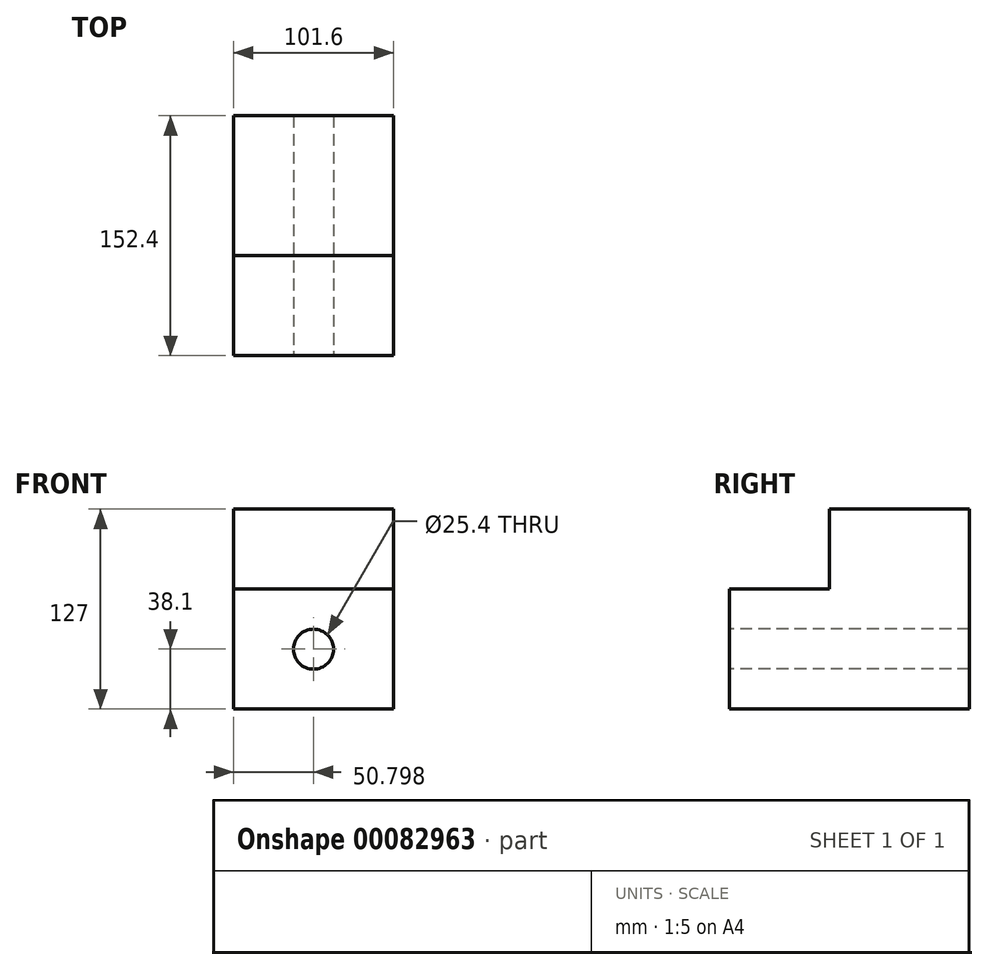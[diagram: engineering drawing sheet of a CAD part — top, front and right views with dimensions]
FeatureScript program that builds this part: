
annotation { "Feature Type Name" : "Feature", "Feature Type Description" : "" }
export const myFeature = defineFeature(function(context is Context, id is Id, definition is map)
    precondition{}
    {
        {
            var Q0;
            Q0=qCreatedBy(makeId("Top.planeOp"),FACE);
            var sketch = newSketch(context, id + "F0", { "sketchPlane" : qUnion([Q0])});
            skLineSegment(sketch, "E0.bottom", {"start": v(-16.71, 112.96) * mm, "end": v(84.89, 112.96) * mm});
            skLineSegment(sketch, "E0.top", {"start": v(-16.71, -39.44) * mm, "end": v(84.89, -39.44) * mm});
            skLineSegment(sketch, "E0.left", {"start": v(-16.71, 112.96) * mm, "end": v(-16.71, -39.44) * mm});
            skLineSegment(sketch, "E0.right", {"start": v(84.89, 112.96) * mm, "end": v(84.89, -39.44) * mm});
            skSolve(sketch);
        }
        {
            var Q0;
            Q0 = qSketchRegion(id + "F0", true);
            extrude(context, id + "F1", {"entities" : qUnion([Q0]), "depth" : 127 * mm});
        }
        {
            var Q0;
            Q0=makeQuery(id+"F1.opExtrude","SWEPT_FACE",FACE,{"disambiguationData":[OSD([sQuery(id+"F0.wireOp",EDGE,"E0.left")])]});
            var sketch = newSketch(context, id + "F2", { "sketchPlane" : qUnion([Q0])});
            skLineSegment(sketch, "E1.bottom", {"start": v(39.44, 127) * mm, "end": v(-24.06, 127) * mm});
            skLineSegment(sketch, "E1.top", {"start": v(39.44, 76.2) * mm, "end": v(-24.06, 76.2) * mm});
            skLineSegment(sketch, "E1.left", {"start": v(39.44, 127) * mm, "end": v(39.44, 76.2) * mm});
            skLineSegment(sketch, "E1.right", {"start": v(-24.06, 127) * mm, "end": v(-24.06, 76.2) * mm});
            skSolve(sketch);
        }
        {
            var Q0;
            Q0 = qSketchRegion(id + "F2", true);
            extrude(context, id + "F3", {"entities" : qUnion([Q0]), "operationType" : NewBodyOperationType.REMOVE, "oppositeDirection" : true, "depth" : 101.6 * mm});
        }
        {
            var Q0;
            Q0=makeQuery(id+"F1.opExtrude","SWEPT_FACE",FACE,{"disambiguationData":[OSD([sQuery(id+"F0.wireOp",EDGE,"E0.top")])]});
            var sketch = newSketch(context, id + "F4", { "sketchPlane" : qUnion([Q0])});
            skCircle(sketch, "E2", {"center": v(34.09, 38.1) * mm, "radius": 12.7 * mm});
            skSolve(sketch);
        }
        {
            var Q0;
            Q0=makeQuery(id+"F4.imprint","IMPRINT",FACE,{"disambiguationData":[TD([[makeQuery(id+"F4.imprint","IMPRINT",EDGE,{"derivedFrom":sQuery(id+"F4.wireOp",EDGE,"E2")}),1.0]])]});
            extrude(context, id + "F5", {"entities" : qUnion([Q0]), "operationType" : NewBodyOperationType.REMOVE, "oppositeDirection" : true, "depth" : 152.4 * mm});
        }
    });
